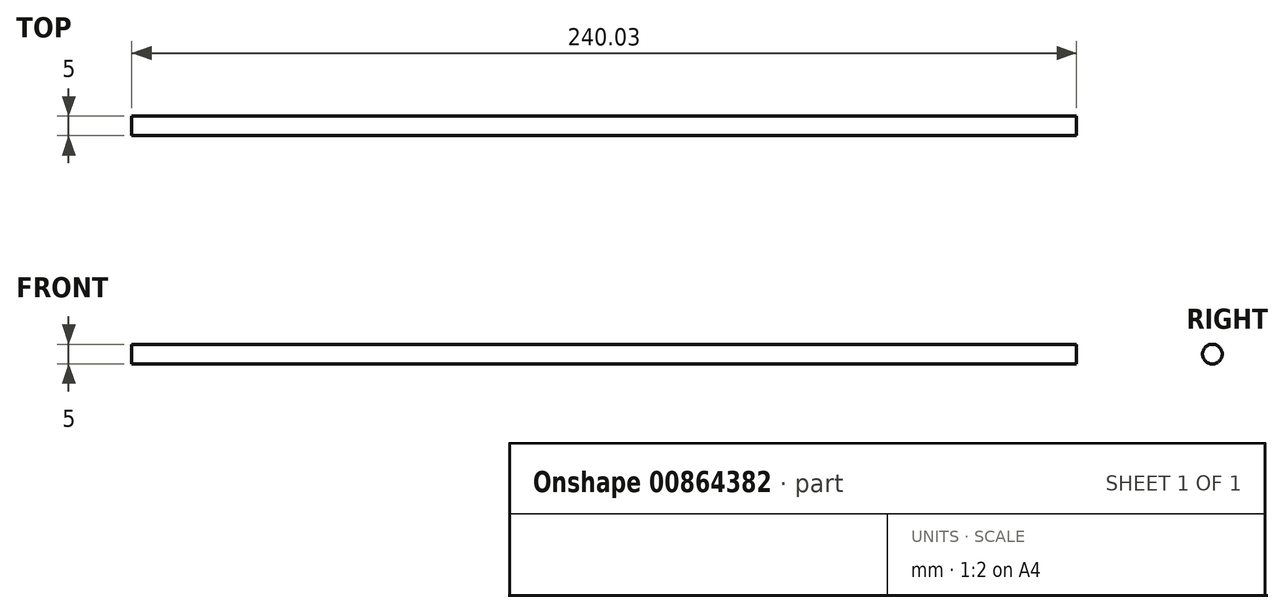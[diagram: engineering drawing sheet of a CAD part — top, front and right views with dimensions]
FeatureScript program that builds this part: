
annotation { "Feature Type Name" : "Feature", "Feature Type Description" : "" }
export const myFeature = defineFeature(function(context is Context, id is Id, definition is map)
    precondition{}
    {
        {
            var Q0;
            Q0=qCreatedBy(makeId("Front.planeOp"),FACE);
            var sketch = newSketch(context, id + "F0", { "sketchPlane" : qUnion([Q0])});
            skLineSegment(sketch, "E0", {"start": v(0, 0) * mm, "end": v(240.03, 0) * mm});
            skSolve(sketch);
        }
        {
            var Q0;
            Q0=qCreatedBy(makeId("Right.planeOp"),FACE);
            var sketch = newSketch(context, id + "F1", { "sketchPlane" : qUnion([Q0])});
            skCircle(sketch, "E1", {"center": v(0, 0) * mm, "radius": 2.5 * mm});
            skSolve(sketch);
        }
        {
            var Q0;
            Q0=makeQuery(id+"F1.imprint","IMPRINT",FACE,{"disambiguationData":[TD([[makeQuery(id+"F1.imprint","IMPRINT",EDGE,{"derivedFrom":sQuery(id+"F1.wireOp",EDGE,"E1")}),1.0]])]});
            var Q1;
            Q1=qConstructionFilter(qBodyType(qCreatedBy(id+"F0",EDGE),BodyType.WIRE),ConstructionObject.NO);
            sweep(context, id + "F2", {"profiles" : qUnion([Q0]), "path" : qUnion([Q1]), "keepProfileOrientation" : true});
        }
    });
